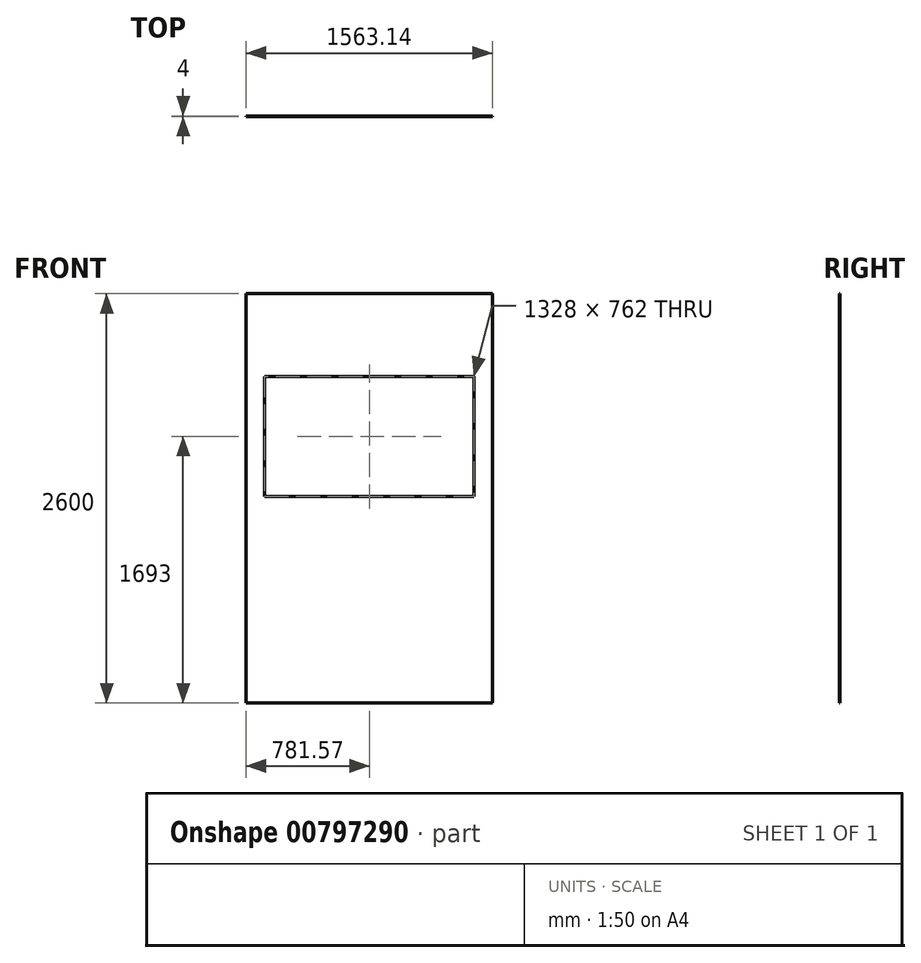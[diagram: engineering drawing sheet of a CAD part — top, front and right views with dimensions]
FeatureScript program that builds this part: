
annotation { "Feature Type Name" : "Feature", "Feature Type Description" : "" }
export const myFeature = defineFeature(function(context is Context, id is Id, definition is map)
    precondition{}
    {
        {
            var Q0;
            Q0=qCreatedBy(makeId("Front.planeOp"),FACE);
            var sketch = newSketch(context, id + "F0", { "sketchPlane" : qUnion([Q0])});
            skLineSegment(sketch, "E0.bottom", {"start": v(781.57, 1300) * mm, "end": v(-781.57, 1300) * mm});
            skLineSegment(sketch, "E0.top", {"start": v(781.57, -1300) * mm, "end": v(-781.57, -1300) * mm});
            skLineSegment(sketch, "E0.left", {"start": v(781.57, 1300) * mm, "end": v(781.57, -1300) * mm});
            skLineSegment(sketch, "E0.right", {"start": v(-781.57, 1300) * mm, "end": v(-781.57, -1300) * mm});
            skPoint(sketch, "E0.middle", {"position": v(0, 0) * mm});
            skLineSegment(sketch, "E1.bottom", {"start": v(664, 774) * mm, "end": v(-664, 774) * mm});
            skLineSegment(sketch, "E1.top", {"start": v(664, 12) * mm, "end": v(-664, 12) * mm});
            skLineSegment(sketch, "E1.left", {"start": v(664, 774) * mm, "end": v(664, 12) * mm});
            skLineSegment(sketch, "E1.right", {"start": v(-664, 774) * mm, "end": v(-664, 12) * mm});
            skPoint(sketch, "E1.middle", {"position": v(0, 393) * mm});
            skPoint(sketch, "E1.middle.positionSnap0", {"position": v(0, 1300) * mm});
            skPoint(sketch, "E1.centerSnap0", {"position": v(0, 1300) * mm});
            skSolve(sketch);
        }
        {
            var Q0;
            Q0 = qSketchRegion(id + "F0", true);
            extrude(context, id + "F1", {"entities" : qUnion([Q0]), "depth" : 4 * mm, "offsetDistance" : 25 * mm, "symmetric" : true});
        }
    });
